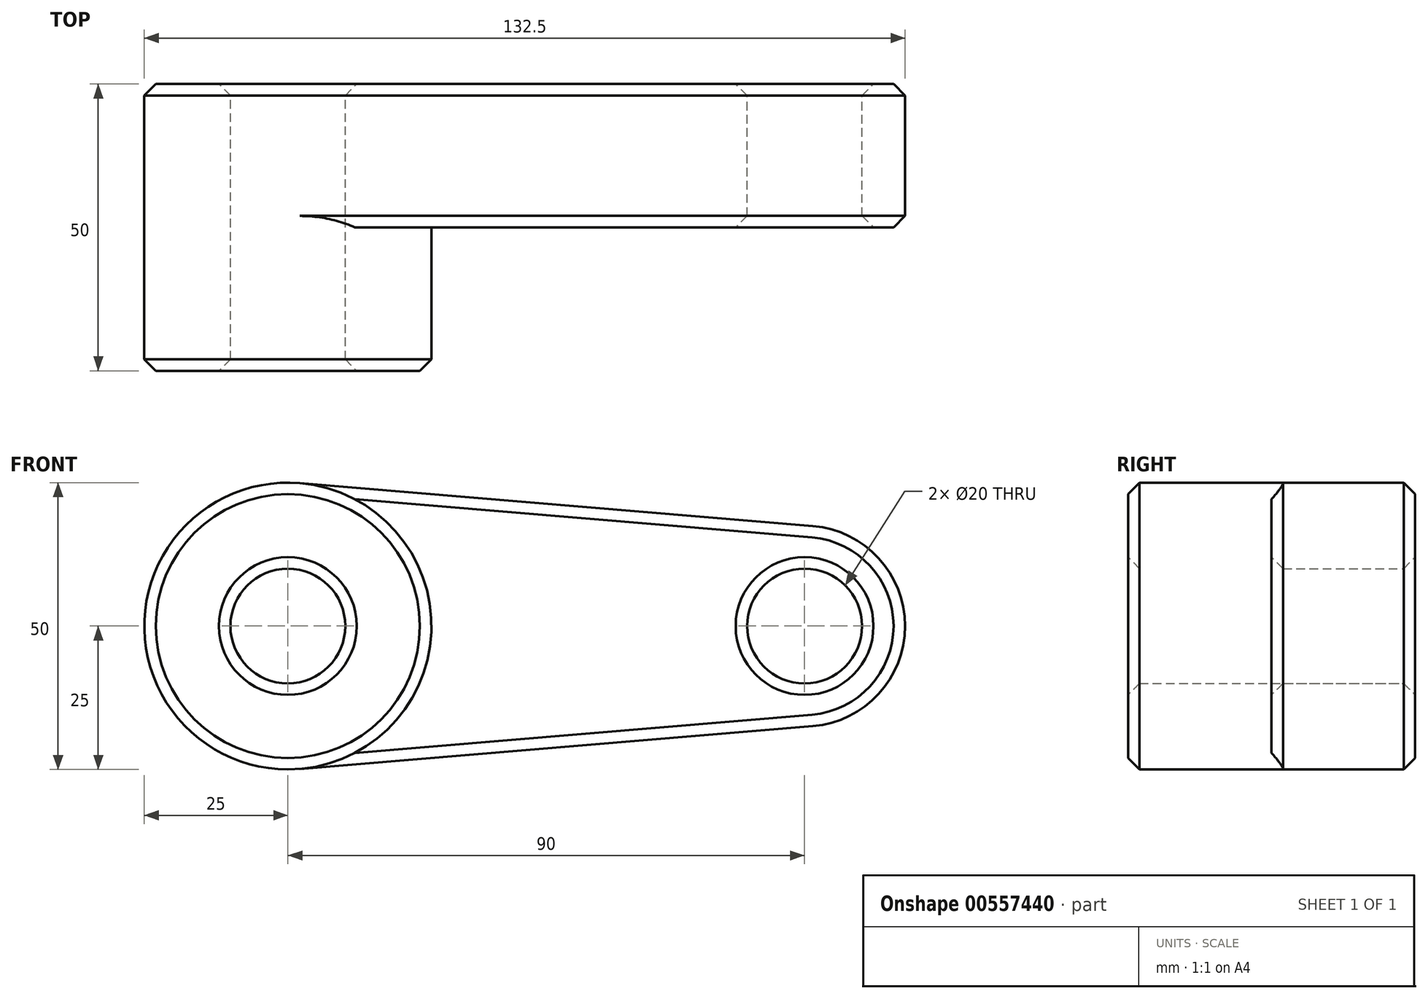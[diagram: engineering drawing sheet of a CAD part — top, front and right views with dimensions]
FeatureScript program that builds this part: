
annotation { "Feature Type Name" : "Feature", "Feature Type Description" : "" }
export const myFeature = defineFeature(function(context is Context, id is Id, definition is map)
    precondition{}
    {
        {
            var Q0;
            Q0=qCreatedBy(makeId("Front.planeOp"),FACE);
            var sketch = newSketch(context, id + "F0", { "sketchPlane" : qUnion([Q0])});
            skCircle(sketch, "E0", {"center": v(0, 0) * mm, "radius": 25 * mm});
            skCircle(sketch, "E1", {"center": v(90, 0) * mm, "radius": 17.5 * mm});
            skLineSegment(sketch, "E2", {"start": v(2.08, 24.91) * mm, "end": v(91.46, 17.44) * mm});
            skLineSegment(sketch, "E3", {"start": v(2.08, -24.91) * mm, "end": v(91.46, -17.44) * mm});
            skCircle(sketch, "E4", {"center": v(0, 0) * mm, "radius": 10 * mm});
            skCircle(sketch, "E5", {"center": v(90, 0) * mm, "radius": 10 * mm});
            skSolve(sketch);
        }
        {
            var Q0;
            Q0 = qSketchRegion(id + "F0", true);
            extrude(context, id + "F1", {"entities" : qUnion([Q0]), "depth" : 25 * mm, "offsetDistance" : 25 * mm});
        }
        {
            var Q0;
            Q0=makeQuery(id+"F0.imprint","IMPRINT",FACE,{"disambiguationData":[TD([[makeQuery(id+"F0.imprint","IMPRINT",EDGE,{"derivedFrom":sQuery(id+"F0.wireOp",EDGE,"E4")}),-1.0]])]});
            extrude(context, id + "F2", {"entities" : qUnion([Q0]), "operationType" : NewBodyOperationType.ADD, "depth" : 50 * mm, "offsetDistance" : 25 * mm});
        }
        {
            var Q0;
            Q0=makeQuery(id+"F2.opExtrude","CAP_EDGE",EDGE,{"disambiguationData":[OSD([sQuery(id+"F0.wireOp",EDGE,"E4")])],"isStart":false});
            var Q1;
            Q1=makeQuery(id+"F2.opExtrude","CAP_EDGE",EDGE,{"disambiguationData":[OSD([sQuery(id+"F0.wireOp",EDGE,"E0")])],"isStart":false});
            var Q2;
            Q2=makeQuery(id+"F1.opExtrude","CAP_EDGE",EDGE,{"disambiguationData":[OSD([sQuery(id+"F0.wireOp",EDGE,"E5")])],"isStart":false});
            chamfer(context, id + "F3", {"entities" : qUnion([Q0, Q1, Q2]), "width" : 2 * mm, "tangentPropagation" : true});
        }
        {
            var Q0;
            Q0=makeQuery(id+"F1.opExtrude","CAP_EDGE",EDGE,{"disambiguationData":[OSD([sQuery(id+"F0.wireOp",EDGE,"E4")])],"isStart":true});
            var Q1;
            Q1=makeQuery(id+"F1.opExtrude","CAP_EDGE",EDGE,{"disambiguationData":[OSD([sQuery(id+"F0.wireOp",EDGE,"E5")])],"isStart":true});
            var Q2;
            Q2=makeQuery(id+"F1.opExtrude","CAP_EDGE",EDGE,{"disambiguationData":[OSD([sQuery(id+"F0.wireOp",EDGE,"E2")])],"isStart":true});
            chamfer(context, id + "F4", {"entities" : qUnion([Q0, Q1, Q2]), "width" : 2 * mm, "tangentPropagation" : true});
        }
        {
            var Q0;
            Q0=makeQuery(id+"F1.opExtrude","CAP_EDGE",EDGE,{"disambiguationData":[OSD([sQuery(id+"F0.wireOp",EDGE,"E3")])],"isStart":false});
            chamfer(context, id + "F5", {"entities" : qUnion([Q0]), "width" : 2 * mm, "tangentPropagation" : true});
        }
    });
